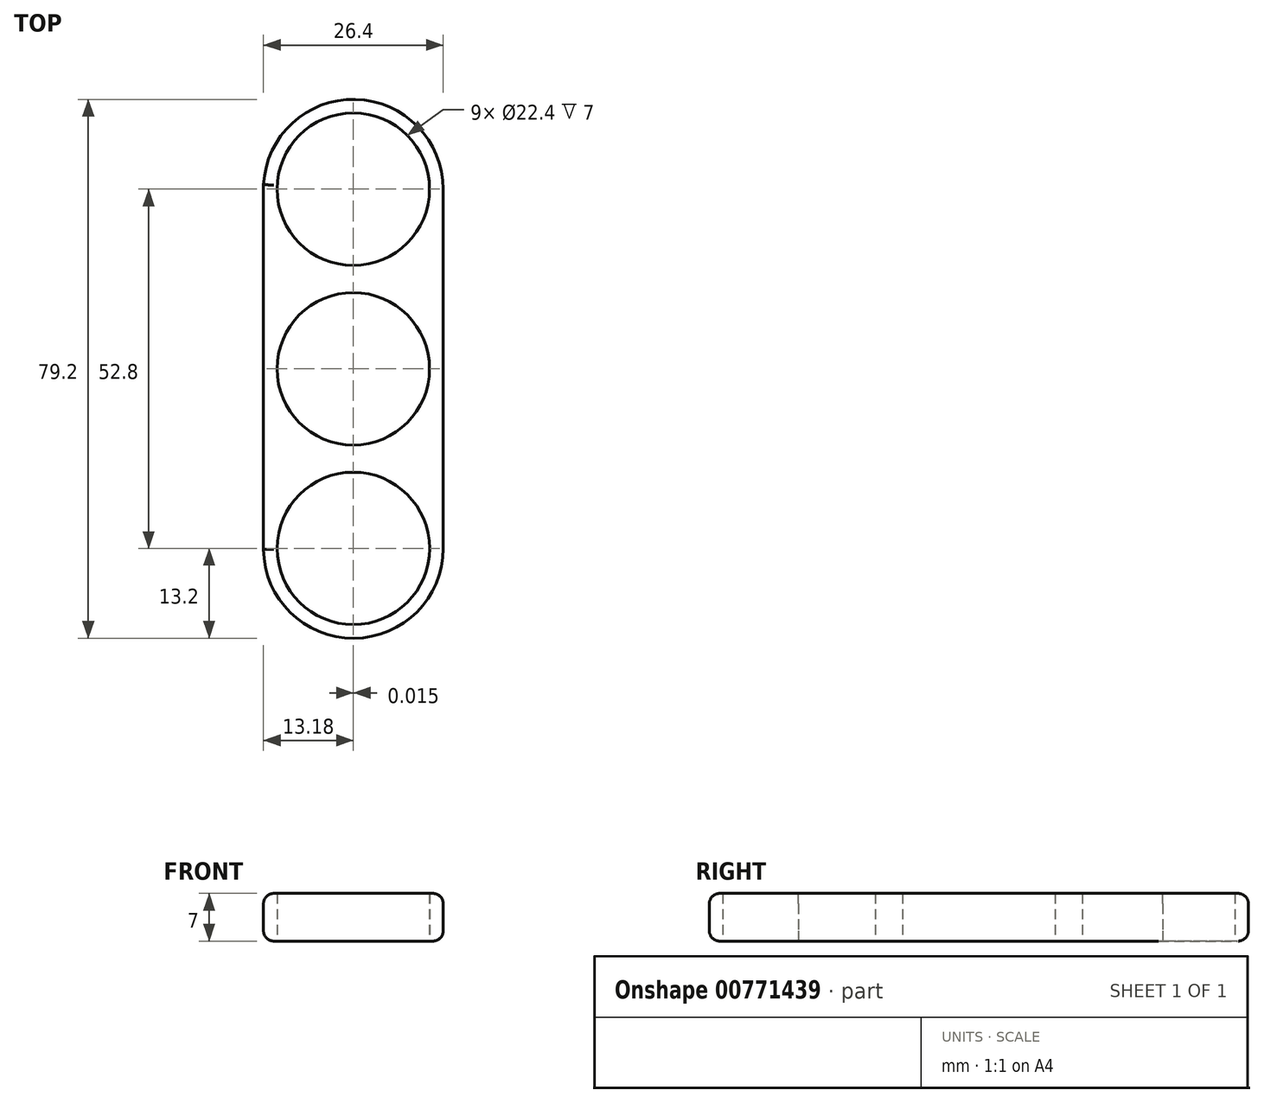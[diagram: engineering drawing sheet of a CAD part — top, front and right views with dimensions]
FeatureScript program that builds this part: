
annotation { "Feature Type Name" : "Feature", "Feature Type Description" : "" }
export const myFeature = defineFeature(function(context is Context, id is Id, definition is map)
    precondition{}
    {
        {
            var Q0;
            Q0=qCreatedBy(makeId("Top.planeOp"),FACE);
            var sketch = newSketch(context, id + "F0", { "sketchPlane" : qUnion([Q0])});
            skCircle(sketch, "E0", {"center": v(0, 0) * mm, "radius": 11.2 * mm});
            skArc(sketch, "E1", {"start": v(-13.18, 0.65) * mm, "mid": v(-13.2, 0) * mm, "end": v(-13.18, -0.65) * mm});
            skCircle(sketch, "E2", {"center": v(0, 26.4) * mm, "radius": 11.2 * mm});
            skArc(sketch, "E3", {"start": v(13.2, 26.4) * mm, "mid": v(-0.32, 39.6) * mm, "end": v(-13.18, 25.75) * mm});
            skCircle(sketch, "E4.1.0", {"center": v(0.02, -26.4) * mm, "radius": 11.2 * mm});
            skArc(sketch, "E4.1.1", {"start": v(-13.18, -26.26) * mm, "mid": v(-0.05, -39.6) * mm, "end": v(13.22, -26.4) * mm});
            skLineSegment(sketch, "E5", {"start": v(-13.18, 27.05) * mm, "end": v(-13.18, -26.54) * mm});
            skLineSegment(sketch, "E6", {"start": v(13.2, 26.4) * mm, "end": v(13.22, -26.4) * mm});
            skSolve(sketch);
        }
        {
            var Q0;
            Q0=makeQuery(id+"F0.imprint","IMPRINT",FACE,{"disambiguationData":[TD([[makeQuery(id+"F0.imprint","IMPRINT",EDGE,{"derivedFrom":sQuery(id+"F0.wireOp",EDGE,"E2")}),-1.0]])]});
            var Q1;
            {var subQ0=sQuery(id+"F0.wireOp",EDGE,"E5");var subQ1=sQuery(id+"F0.wireOp",EDGE,"E1");var subQ2=makeQuery(id+"F0.imprint","INTERSECT",VERTEX,{"disambiguationData":[OD(0.0)],"derivedFrom":[subQ1,subQ0]});Q1=makeQuery(id+"F0.imprint","IMPRINT",FACE,{"disambiguationData":[TD([[makeQuery(id+"F0.imprint","IMPRINT",EDGE,{"disambiguationData":[TD([[subQ2,1.0]])],"derivedFrom":subQ1}),-1.0]])]});}
            var Q2;
            {var subQ5=sQuery(id+"F0.wireOp",EDGE,"E6");Q2=makeQuery(id+"F0.imprint","IMPRINT",FACE,{"disambiguationData":[TD([[makeQuery(id+"F0.imprint","IMPRINT",EDGE,{"derivedFrom":subQ5}),-1.0]])]});}
            var Q3;
            Q3=makeQuery(id+"F0.imprint","IMPRINT",FACE,{"disambiguationData":[TD([[makeQuery(id+"F0.imprint","IMPRINT",EDGE,{"derivedFrom":sQuery(id+"F0.wireOp",EDGE,"E0")}),-1.0]])]});
            var Q4;
            {var subQ0=sQuery(id+"F0.wireOp",EDGE,"E5");var subQ1=sQuery(id+"F0.wireOp",EDGE,"E1");var subQ2=makeQuery(id+"F0.imprint","INTERSECT",VERTEX,{"disambiguationData":[OD(1.0)],"derivedFrom":[subQ1,subQ0]});Q4=makeQuery(id+"F0.imprint","IMPRINT",FACE,{"disambiguationData":[TD([[makeQuery(id+"F0.imprint","IMPRINT",EDGE,{"disambiguationData":[TD([[subQ2,-1.0]])],"derivedFrom":subQ1}),-1.0]])]});}
            var Q5;
            Q5=makeQuery(id+"F0.imprint","IMPRINT",FACE,{"disambiguationData":[TD([[makeQuery(id+"F0.imprint","IMPRINT",EDGE,{"derivedFrom":sQuery(id+"F0.wireOp",EDGE,"E4.1.0")}),-1.0]])]});
            extrude(context, id + "F1", {"entities" : qUnion([Q0, Q1, Q2, Q3, Q4, Q5]), "depth" : 7 * mm, "offsetDistance" : 25 * mm});
        }
        {
            var Q0;
            Q0=makeQuery(id+"F1.opExtrude","CAP_EDGE",EDGE,{"disambiguationData":[OSD([sQuery(id+"F0.wireOp",EDGE,"E4.1.1")])],"isStart":true});
            var Q1;
            Q1=makeQuery(id+"F1.opExtrude","CAP_EDGE",EDGE,{"disambiguationData":[OSD([sQuery(id+"F0.wireOp",EDGE,"E3")])],"isStart":true});
            var Q2;
            Q2=makeQuery(id+"F1.opExtrude","CAP_EDGE",EDGE,{"disambiguationData":[OSD([sQuery(id+"F0.wireOp",EDGE,"E3")])],"isStart":false});
            var Q3;
            Q3=makeQuery(id+"F1.opExtrude","CAP_EDGE",EDGE,{"disambiguationData":[OSD([sQuery(id+"F0.wireOp",EDGE,"E5")])],"isStart":false});
            var Q4;
            Q4=makeQuery(id+"F1.opExtrude","CAP_EDGE",EDGE,{"disambiguationData":[OSD([sQuery(id+"F0.wireOp",EDGE,"E6")])],"isStart":false});
            var Q5;
            Q5=makeQuery(id+"F1.opExtrude","CAP_EDGE",EDGE,{"disambiguationData":[OSD([sQuery(id+"F0.wireOp",EDGE,"E6")])],"isStart":true});
            var Q6;
            Q6=makeQuery(id+"F1.opExtrude","CAP_EDGE",EDGE,{"disambiguationData":[OSD([sQuery(id+"F0.wireOp",EDGE,"E5")])],"isStart":true});
            var Q7;
            Q7=makeQuery(id+"F1.opExtrude","CAP_EDGE",EDGE,{"disambiguationData":[OSD([sQuery(id+"F0.wireOp",EDGE,"E4.1.1")])],"isStart":false});
            fillet(context, id + "F2", {"entities" : qUnion([Q0, Q1, Q2, Q3, Q4, Q5, Q6, Q7]), "radius" : 1.5 * mm, "tangentPropagation" : true, "allowEdgeOverflow" : false});
        }
    });
